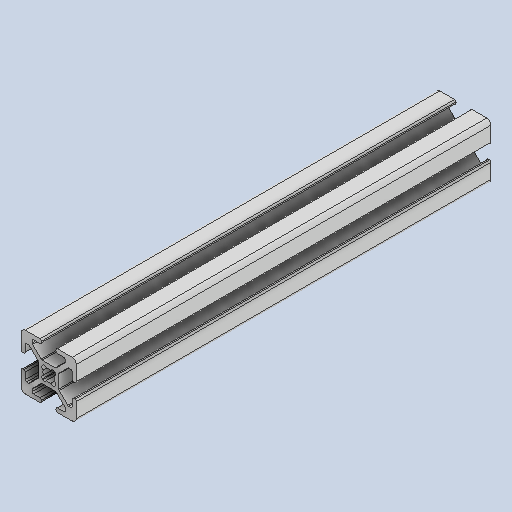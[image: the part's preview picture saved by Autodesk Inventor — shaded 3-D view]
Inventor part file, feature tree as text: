
AUTODESK INVENTOR PART (.ipt)
format: ipt  version: 2022 (Build 260153000, 153)  size: 299,520 bytes
history: native  units: in
note: dims shown in document units (in); Inventor stores cm internally (conversion verified against a paired STEP export)
features: other x3, sketch x1
ambient origin geometry x8: Origin, YZ Plane, XZ Plane, XY Plane, X Axis, Y Axis, Z Axis, Center Point
bodies: Solid1 (feature_tree)
feature tree (4):
  other  "20x20x150 T Slot Extrusion Bar.ipt"
  other  "Solid1::20x20x150 T Slot Extrusion Bar.ipt"
  other  "TaggingFeature1"
  sketch  "Sketch_1"  dims[d0=0.3937in]
